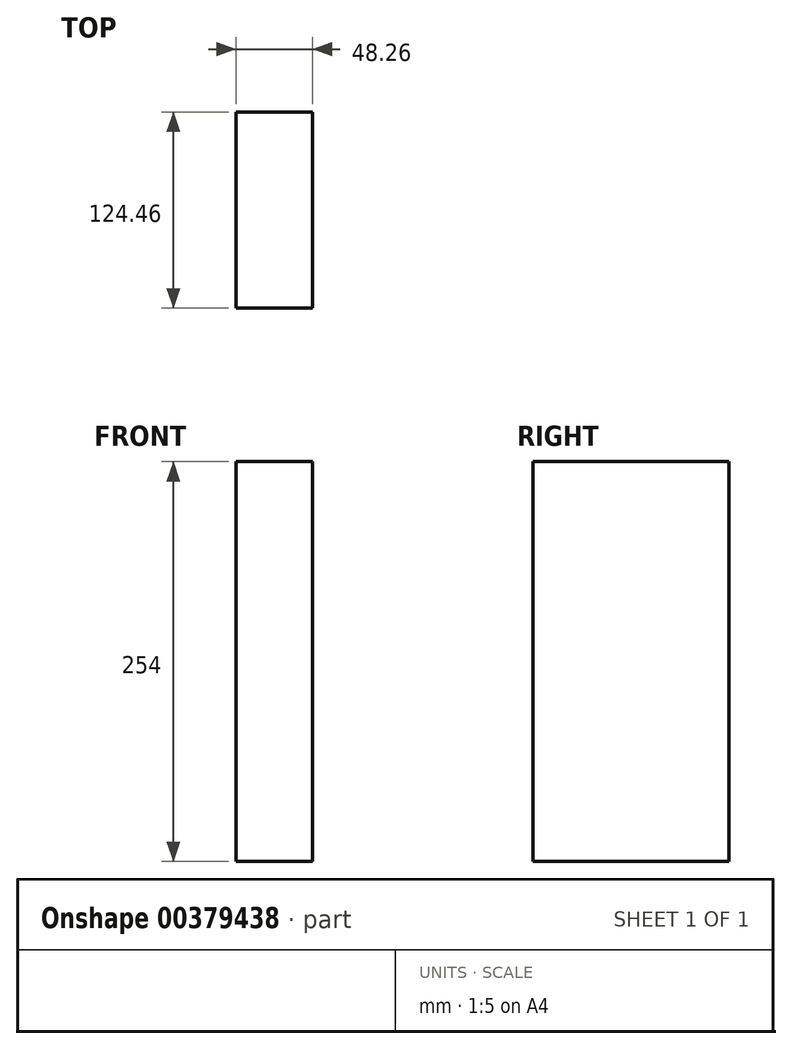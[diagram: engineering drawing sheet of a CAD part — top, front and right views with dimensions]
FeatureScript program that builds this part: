
annotation { "Feature Type Name" : "Feature", "Feature Type Description" : "" }
export const myFeature = defineFeature(function(context is Context, id is Id, definition is map)
    precondition{}
    {
        {
            var Q0;
            Q0=qCreatedBy(makeId("Top.planeOp"),FACE);
            var sketch = newSketch(context, id + "F0", { "sketchPlane" : qUnion([Q0])});
            skLineSegment(sketch, "E0.bottom", {"start": v(-19.23, -104.65) * mm, "end": v(-67.5, -104.65) * mm});
            skLineSegment(sketch, "E0.top", {"start": v(-19.23, 19.81) * mm, "end": v(-67.5, 19.81) * mm});
            skLineSegment(sketch, "E0.left", {"start": v(-19.23, -104.65) * mm, "end": v(-19.23, 19.81) * mm});
            skLineSegment(sketch, "E0.right", {"start": v(-67.5, -104.65) * mm, "end": v(-67.5, 19.81) * mm});
            skSolve(sketch);
        }
        {
            var Q0;
            Q0=makeQuery(id+"F0.imprint","IMPRINT",FACE,{"disambiguationData":[TD([[makeQuery(id+"F0.imprint","IMPRINT",EDGE,{"derivedFrom":sQuery(id+"F0.wireOp",EDGE,"E0.bottom")}),-1.0]])]});
            extrude(context, id + "F1", {"entities" : qUnion([Q0]), "depth" : 127 * mm, "hasSecondDirection" : true, "secondDirectionOppositeDirection" : true, "secondDirectionDepth" : 127 * mm});
        }
    });
